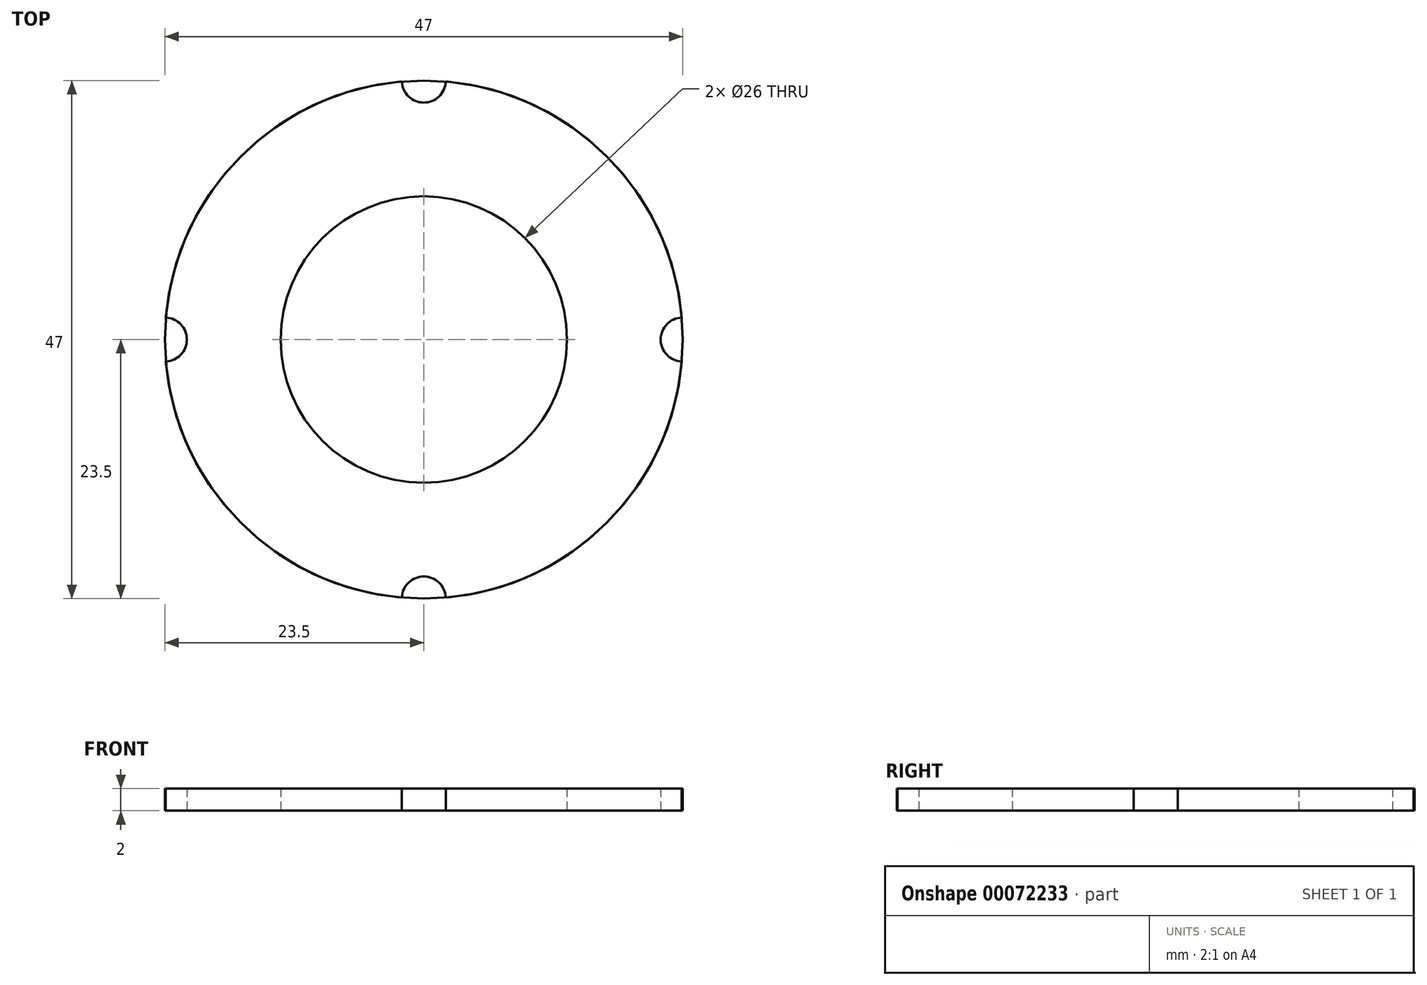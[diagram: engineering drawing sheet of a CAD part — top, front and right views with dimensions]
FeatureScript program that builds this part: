
annotation { "Feature Type Name" : "Feature", "Feature Type Description" : "" }
export const myFeature = defineFeature(function(context is Context, id is Id, definition is map)
    precondition{}
    {
        {
            var Q0;
            Q0=qCreatedBy(makeId("Top.planeOp"),FACE);
            var sketch = newSketch(context, id + "F0", { "sketchPlane" : qUnion([Q0])});
            skCircle(sketch, "E0", {"center": v(0, 0) * mm, "radius": 23.5 * mm});
            skCircle(sketch, "E1", {"center": v(0, 0) * mm, "radius": 21.5 * mm});
            skCircle(sketch, "E2", {"center": v(0, 0) * mm, "radius": 13 * mm});
            skCircle(sketch, "E3", {"center": v(0, 23.5) * mm, "radius": 2 * mm});
            skCircle(sketch, "E4", {"center": v(23.5, 0) * mm, "radius": 2 * mm});
            skCircle(sketch, "E5", {"center": v(0, -23.5) * mm, "radius": 2 * mm});
            skCircle(sketch, "E6", {"center": v(-23.5, 0) * mm, "radius": 2 * mm});
            skSolve(sketch);
        }
        {
            var Q0;
            Q0=makeQuery(id+"F0.imprint","IMPRINT",FACE,{"disambiguationData":[TD([[makeQuery(id+"F0.imprint","IMPRINT",EDGE,{"derivedFrom":sQuery(id+"F0.wireOp",EDGE,"E0")}),1.0]])]});
            var Q1;
            Q1=makeQuery(id+"F0.imprint","IMPRINT",FACE,{"disambiguationData":[TD([[makeQuery(id+"F0.imprint","IMPRINT",EDGE,{"derivedFrom":sQuery(id+"F0.wireOp",EDGE,"E1")}),1.0]])]});
            var Q2;
            {var subQ0=sQuery(id+"F0.wireOp",EDGE,"NTugGdlW-D3lf-hBSn-7u8i-5yiG6s04YJxx");var subQ1=sQuery(id+"F0.wireOp",EDGE,"E1");var subQ2=makeQuery(id+"F0.imprint","INTERSECT",VERTEX,{"disambiguationData":[OD(0.0)],"derivedFrom":[subQ1,subQ0]});Q2=makeQuery(id+"F0.imprint","IMPRINT",FACE,{"disambiguationData":[TD([[makeQuery(id+"F0.imprint","IMPRINT",EDGE,{"disambiguationData":[TD([[subQ2,-1.0]])],"derivedFrom":subQ1}),-1.0]])]});}
            var Q3;
            {var subQ0=sQuery(id+"F0.wireOp",EDGE,"NTugGdlW-D3lf-hBSn-7u8i-5yiG6s04YJxx");var subQ1=sQuery(id+"F0.wireOp",EDGE,"E1");var subQ2=makeQuery(id+"F0.imprint","INTERSECT",VERTEX,{"disambiguationData":[OD(0.0)],"derivedFrom":[subQ1,subQ0]});Q3=makeQuery(id+"F0.imprint","IMPRINT",FACE,{"disambiguationData":[TD([[makeQuery(id+"F0.imprint","IMPRINT",EDGE,{"disambiguationData":[TD([[subQ2,-1.0]])],"derivedFrom":subQ1}),1.0]])]});}
            var Q4;
            {var subQ0=sQuery(id+"F0.wireOp",EDGE,"ZNEsYzks-agGc-lyrO-R8pg-LjK3S9Cqd63Q");var subQ1=sQuery(id+"F0.wireOp",EDGE,"E1");var subQ2=makeQuery(id+"F0.imprint","INTERSECT",VERTEX,{"disambiguationData":[OD(0.0)],"derivedFrom":[subQ1,subQ0]});Q4=makeQuery(id+"F0.imprint","IMPRINT",FACE,{"disambiguationData":[TD([[makeQuery(id+"F0.imprint","IMPRINT",EDGE,{"disambiguationData":[TD([[subQ2,1.0]])],"derivedFrom":subQ1}),1.0]])]});}
            var Q5;
            {var subQ0=sQuery(id+"F0.wireOp",EDGE,"ZNEsYzks-agGc-lyrO-R8pg-LjK3S9Cqd63Q");var subQ1=sQuery(id+"F0.wireOp",EDGE,"E1");var subQ2=makeQuery(id+"F0.imprint","INTERSECT",VERTEX,{"disambiguationData":[OD(0.0)],"derivedFrom":[subQ1,subQ0]});Q5=makeQuery(id+"F0.imprint","IMPRINT",FACE,{"disambiguationData":[TD([[makeQuery(id+"F0.imprint","IMPRINT",EDGE,{"disambiguationData":[TD([[subQ2,1.0]])],"derivedFrom":subQ1}),-1.0]])]});}
            var Q6;
            {var subQ0=sQuery(id+"F0.wireOp",EDGE,"3NnAhz3W-eDMg-tC0v-c5uH-hHy52S0xp06p");var subQ1=sQuery(id+"F0.wireOp",EDGE,"E1");var subQ2=makeQuery(id+"F0.imprint","INTERSECT",VERTEX,{"disambiguationData":[OD(0.0)],"derivedFrom":[subQ1,subQ0]});Q6=makeQuery(id+"F0.imprint","IMPRINT",FACE,{"disambiguationData":[TD([[makeQuery(id+"F0.imprint","IMPRINT",EDGE,{"disambiguationData":[TD([[subQ2,-1.0]])],"derivedFrom":subQ1}),-1.0]])]});}
            var Q7;
            {var subQ0=sQuery(id+"F0.wireOp",EDGE,"3xoAh3wH-b0jI-bz4x-s0Ju-uXcoo3OunpsO");var subQ1=sQuery(id+"F0.wireOp",EDGE,"E1");var subQ2=makeQuery(id+"F0.imprint","INTERSECT",VERTEX,{"disambiguationData":[OD(0.0)],"derivedFrom":[subQ1,subQ0]});Q7=makeQuery(id+"F0.imprint","IMPRINT",FACE,{"disambiguationData":[TD([[makeQuery(id+"F0.imprint","IMPRINT",EDGE,{"disambiguationData":[TD([[subQ2,-1.0]])],"derivedFrom":subQ1}),1.0]])]});}
            var Q8;
            {var subQ0=sQuery(id+"F0.wireOp",EDGE,"3xoAh3wH-b0jI-bz4x-s0Ju-uXcoo3OunpsO");var subQ1=sQuery(id+"F0.wireOp",EDGE,"E1");var subQ2=makeQuery(id+"F0.imprint","INTERSECT",VERTEX,{"disambiguationData":[OD(0.0)],"derivedFrom":[subQ1,subQ0]});Q8=makeQuery(id+"F0.imprint","IMPRINT",FACE,{"disambiguationData":[TD([[makeQuery(id+"F0.imprint","IMPRINT",EDGE,{"disambiguationData":[TD([[subQ2,-1.0]])],"derivedFrom":subQ1}),-1.0]])]});}
            var Q9;
            {var subQ0=sQuery(id+"F0.wireOp",EDGE,"3NnAhz3W-eDMg-tC0v-c5uH-hHy52S0xp06p");var subQ1=sQuery(id+"F0.wireOp",EDGE,"E1");var subQ2=makeQuery(id+"F0.imprint","INTERSECT",VERTEX,{"disambiguationData":[OD(0.0)],"derivedFrom":[subQ1,subQ0]});Q9=makeQuery(id+"F0.imprint","IMPRINT",FACE,{"disambiguationData":[TD([[makeQuery(id+"F0.imprint","IMPRINT",EDGE,{"disambiguationData":[TD([[subQ2,-1.0]])],"derivedFrom":subQ1}),1.0]])]});}
            extrude(context, id + "F1", {"entities" : qUnion([Q0, Q1, Q2, Q3, Q4, Q5, Q6, Q7, Q8, Q9]), "depth" : 2 * mm});
        }
        {
            var Q0;
            Q0=makeQuery(id+"F0.imprint","IMPRINT",FACE,{"disambiguationData":[TD([[makeQuery(id+"F0.imprint","IMPRINT",EDGE,{"derivedFrom":sQuery(id+"F0.wireOp",EDGE,"E2")}),-1.0]])]});
            var Q1;
            {var subQ0=sQuery(id+"F0.wireOp",EDGE,"E6");var subQ1=sQuery(id+"F0.wireOp",EDGE,"E0");var subQ2=makeQuery(id+"F0.imprint","INTERSECT",VERTEX,{"disambiguationData":[OD(1.0)],"derivedFrom":[subQ1,subQ0]});Q1=makeQuery(id+"F0.imprint","IMPRINT",FACE,{"disambiguationData":[TD([[makeQuery(id+"F0.imprint","IMPRINT",EDGE,{"disambiguationData":[TD([[subQ2,-1.0]])],"derivedFrom":subQ1}),1.0]])]});}
            var Q2;
            {var subQ0=sQuery(id+"F0.wireOp",EDGE,"E3");var subQ1=sQuery(id+"F0.wireOp",EDGE,"E0");var subQ2=makeQuery(id+"F0.imprint","INTERSECT",VERTEX,{"disambiguationData":[OD(1.0)],"derivedFrom":[subQ1,subQ0]});Q2=makeQuery(id+"F0.imprint","IMPRINT",FACE,{"disambiguationData":[TD([[makeQuery(id+"F0.imprint","IMPRINT",EDGE,{"disambiguationData":[TD([[subQ2,-1.0]])],"derivedFrom":subQ1}),1.0]])]});}
            var Q3;
            {var subQ0=sQuery(id+"F0.wireOp",EDGE,"E5");var subQ1=sQuery(id+"F0.wireOp",EDGE,"E0");var subQ2=makeQuery(id+"F0.imprint","INTERSECT",VERTEX,{"disambiguationData":[OD(1.0)],"derivedFrom":[subQ1,subQ0]});Q3=makeQuery(id+"F0.imprint","IMPRINT",FACE,{"disambiguationData":[TD([[makeQuery(id+"F0.imprint","IMPRINT",EDGE,{"disambiguationData":[TD([[subQ2,-1.0]])],"derivedFrom":subQ1}),1.0]])]});}
            var Q4;
            {var subQ0=sQuery(id+"F0.wireOp",EDGE,"E3");var subQ1=sQuery(id+"F0.wireOp",EDGE,"E0");var subQ2=makeQuery(id+"F0.imprint","INTERSECT",VERTEX,{"disambiguationData":[OD(0.0)],"derivedFrom":[subQ1,subQ0]});Q4=makeQuery(id+"F0.imprint","IMPRINT",FACE,{"disambiguationData":[TD([[makeQuery(id+"F0.imprint","IMPRINT",EDGE,{"disambiguationData":[TD([[subQ2,1.0]])],"derivedFrom":subQ1}),1.0]])]});}
            extrude(context, id + "F2", {"entities" : qUnion([Q0, Q1, Q2, Q3, Q4]), "depth" : 2 * mm});
        }
    });
